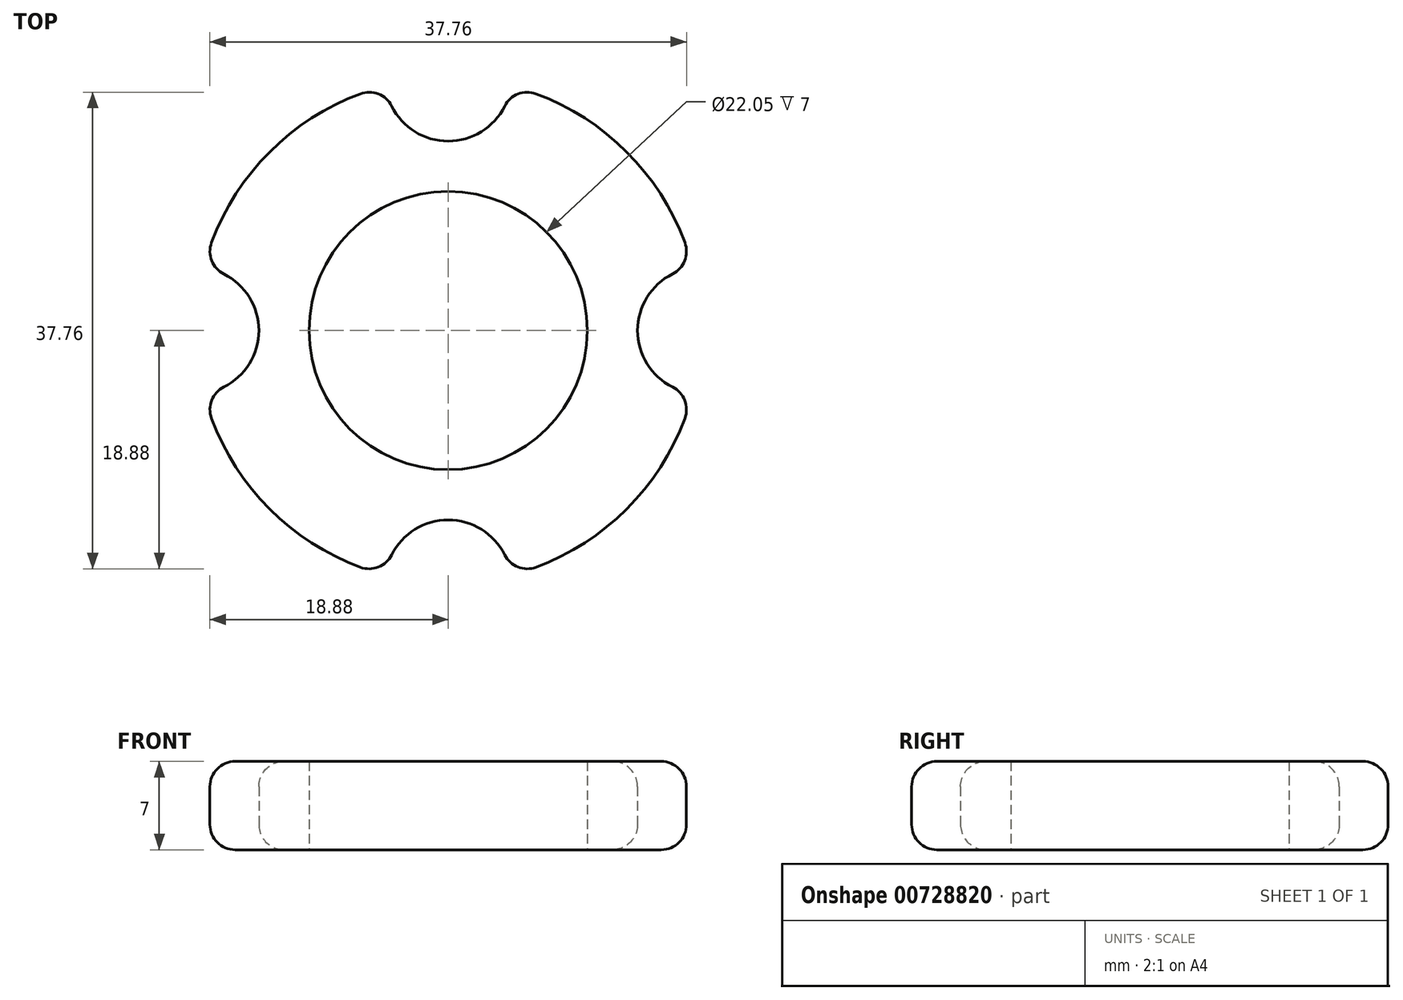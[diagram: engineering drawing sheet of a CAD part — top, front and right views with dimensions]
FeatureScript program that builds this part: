
annotation { "Feature Type Name" : "Feature", "Feature Type Description" : "" }
export const myFeature = defineFeature(function(context is Context, id is Id, definition is map)
    precondition{}
    {
        {
            var Q0;
            Q0=qCreatedBy(makeId("Top.planeOp"),FACE);
            var sketch = newSketch(context, id + "F0", { "sketchPlane" : qUnion([Q0])});
            skCircle(sketch, "E0", {"center": v(0, 0) * mm, "radius": 11.03 * mm});
            skCircle(sketch, "E1", {"center": v(0, 0) * mm, "radius": 20 * mm});
            skCircle(sketch, "E2", {"center": v(0, 20) * mm, "radius": 5 * mm});
            skCircle(sketch, "E3", {"center": v(20, 0) * mm, "radius": 5 * mm});
            skCircle(sketch, "E4", {"center": v(0, -20) * mm, "radius": 5 * mm});
            skCircle(sketch, "E5", {"center": v(-20, 0) * mm, "radius": 5 * mm});
            skSolve(sketch);
        }
        {
            var Q0;
            Q0=makeQuery(id+"F0.imprint","IMPRINT",FACE,{"disambiguationData":[TD([[makeQuery(id+"F0.imprint","IMPRINT",EDGE,{"derivedFrom":sQuery(id+"F0.wireOp",EDGE,"E0")}),-1.0]])]});
            extrude(context, id + "F1", {"entities" : qUnion([Q0]), "depth" : 7 * mm, "offsetDistance" : 25 * mm});
        }
        {
            var Q0;
            {var subQ0=sQuery(id+"F0.wireOp",EDGE,"E1");Q0=makeQuery(id+"F1.opExtrude","CAP_EDGE",EDGE,{"disambiguationData":[OSD([subQ0]),TDD([makeQuery(id+"F0.imprint","IMPRINT",EDGE,{"disambiguationData":[TD([[makeQuery(id+"F0.imprint","INTERSECT",VERTEX,{"disambiguationData":[OD(1.0)],"derivedFrom":[subQ0,sQuery(id+"F0.wireOp",EDGE,"E4")]}),-1.0]])],"derivedFrom":subQ0})])],"isStart":false});}
            var Q1;
            Q1=makeQuery(id+"F1.opExtrude","CAP_EDGE",EDGE,{"disambiguationData":[OSD([sQuery(id+"F0.wireOp",EDGE,"E4")])],"isStart":false});
            var Q2;
            {var subQ0=sQuery(id+"F0.wireOp",EDGE,"E1");Q2=makeQuery(id+"F1.opExtrude","CAP_EDGE",EDGE,{"disambiguationData":[OSD([subQ0]),TDD([makeQuery(id+"F0.imprint","IMPRINT",EDGE,{"disambiguationData":[TD([[makeQuery(id+"F0.imprint","INTERSECT",VERTEX,{"disambiguationData":[OD(1.0)],"derivedFrom":[subQ0,sQuery(id+"F0.wireOp",EDGE,"E5")]}),-1.0]])],"derivedFrom":subQ0})])],"isStart":false});}
            var Q3;
            Q3=makeQuery(id+"F1.opExtrude","CAP_EDGE",EDGE,{"disambiguationData":[OSD([sQuery(id+"F0.wireOp",EDGE,"E5")])],"isStart":false});
            var Q4;
            {var subQ0=sQuery(id+"F0.wireOp",EDGE,"E1");Q4=makeQuery(id+"F1.opExtrude","CAP_EDGE",EDGE,{"disambiguationData":[OSD([subQ0]),TDD([makeQuery(id+"F0.imprint","IMPRINT",EDGE,{"disambiguationData":[TD([[makeQuery(id+"F0.imprint","INTERSECT",VERTEX,{"disambiguationData":[OD(1.0)],"derivedFrom":[subQ0,sQuery(id+"F0.wireOp",EDGE,"E2")]}),-1.0]])],"derivedFrom":subQ0})])],"isStart":false});}
            var Q5;
            Q5=makeQuery(id+"F1.opExtrude","CAP_EDGE",EDGE,{"disambiguationData":[OSD([sQuery(id+"F0.wireOp",EDGE,"E2")])],"isStart":false});
            var Q6;
            {var subQ0=sQuery(id+"F0.wireOp",EDGE,"E1");Q6=makeQuery(id+"F1.opExtrude","CAP_EDGE",EDGE,{"disambiguationData":[OSD([subQ0]),TDD([makeQuery(id+"F0.imprint","IMPRINT",EDGE,{"disambiguationData":[TD([[makeQuery(id+"F0.imprint","INTERSECT",VERTEX,{"disambiguationData":[OD(0.0)],"derivedFrom":[subQ0,sQuery(id+"F0.wireOp",EDGE,"E2")]}),1.0]])],"derivedFrom":subQ0})])],"isStart":false});}
            var Q7;
            Q7=makeQuery(id+"F1.opExtrude","CAP_EDGE",EDGE,{"disambiguationData":[OSD([sQuery(id+"F0.wireOp",EDGE,"E3")])],"isStart":false});
            var Q8;
            {var subQ0=sQuery(id+"F0.wireOp",EDGE,"E4");var subQ1=sQuery(id+"F0.wireOp",EDGE,"E1");Q8=makeQuery(id+"F1.opExtrude","SWEPT_EDGE",EDGE,{"disambiguationData":[OSD([subQ1,subQ0]),TDD([makeQuery(id+"F0.imprint","INTERSECT",VERTEX,{"disambiguationData":[OD(0.0)],"derivedFrom":[subQ1,subQ0]})])]});}
            var Q9;
            {var subQ0=sQuery(id+"F0.wireOp",EDGE,"E4");var subQ1=sQuery(id+"F0.wireOp",EDGE,"E1");Q9=makeQuery(id+"F1.opExtrude","SWEPT_EDGE",EDGE,{"disambiguationData":[OSD([subQ1,subQ0]),TDD([makeQuery(id+"F0.imprint","INTERSECT",VERTEX,{"disambiguationData":[OD(1.0)],"derivedFrom":[subQ1,subQ0]})])]});}
            var Q10;
            {var subQ0=sQuery(id+"F0.wireOp",EDGE,"E1");Q10=makeQuery(id+"F1.opExtrude","CAP_EDGE",EDGE,{"disambiguationData":[OSD([subQ0]),TDD([makeQuery(id+"F0.imprint","IMPRINT",EDGE,{"disambiguationData":[TD([[makeQuery(id+"F0.imprint","INTERSECT",VERTEX,{"disambiguationData":[OD(1.0)],"derivedFrom":[subQ0,sQuery(id+"F0.wireOp",EDGE,"E4")]}),-1.0]])],"derivedFrom":subQ0})])],"isStart":true});}
            var Q11;
            Q11=makeQuery(id+"F1.opExtrude","CAP_EDGE",EDGE,{"disambiguationData":[OSD([sQuery(id+"F0.wireOp",EDGE,"E4")])],"isStart":true});
            var Q12;
            {var subQ0=sQuery(id+"F0.wireOp",EDGE,"E1");Q12=makeQuery(id+"F1.opExtrude","CAP_EDGE",EDGE,{"disambiguationData":[OSD([subQ0]),TDD([makeQuery(id+"F0.imprint","IMPRINT",EDGE,{"disambiguationData":[TD([[makeQuery(id+"F0.imprint","INTERSECT",VERTEX,{"disambiguationData":[OD(1.0)],"derivedFrom":[subQ0,sQuery(id+"F0.wireOp",EDGE,"E5")]}),-1.0]])],"derivedFrom":subQ0})])],"isStart":true});}
            var Q13;
            {var subQ0=sQuery(id+"F0.wireOp",EDGE,"E1");Q13=makeQuery(id+"F1.opExtrude","SWEPT_FACE",FACE,{"disambiguationData":[OSD([subQ0]),TDD([makeQuery(id+"F0.imprint","IMPRINT",EDGE,{"disambiguationData":[TD([[makeQuery(id+"F0.imprint","INTERSECT",VERTEX,{"disambiguationData":[OD(1.0)],"derivedFrom":[subQ0,sQuery(id+"F0.wireOp",EDGE,"E4")]}),-1.0]])],"derivedFrom":subQ0})])]});}
            var Q14;
            Q14=makeQuery(id+"F1.opExtrude","CAP_EDGE",EDGE,{"disambiguationData":[OSD([sQuery(id+"F0.wireOp",EDGE,"E3")])],"isStart":true});
            var Q15;
            {var subQ0=sQuery(id+"F0.wireOp",EDGE,"E3");var subQ1=sQuery(id+"F0.wireOp",EDGE,"E1");Q15=makeQuery(id+"F1.opExtrude","SWEPT_EDGE",EDGE,{"disambiguationData":[OSD([subQ1,subQ0]),TDD([makeQuery(id+"F0.imprint","INTERSECT",VERTEX,{"disambiguationData":[OD(0.0)],"derivedFrom":[subQ1,subQ0]})])]});}
            var Q16;
            {var subQ0=sQuery(id+"F0.wireOp",EDGE,"E1");Q16=makeQuery(id+"F1.opExtrude","CAP_EDGE",EDGE,{"disambiguationData":[OSD([subQ0]),TDD([makeQuery(id+"F0.imprint","IMPRINT",EDGE,{"disambiguationData":[TD([[makeQuery(id+"F0.imprint","INTERSECT",VERTEX,{"disambiguationData":[OD(0.0)],"derivedFrom":[subQ0,sQuery(id+"F0.wireOp",EDGE,"E2")]}),1.0]])],"derivedFrom":subQ0})])],"isStart":true});}
            var Q17;
            Q17=makeQuery(id+"F1.opExtrude","CAP_EDGE",EDGE,{"disambiguationData":[OSD([sQuery(id+"F0.wireOp",EDGE,"E2")])],"isStart":true});
            var Q18;
            {var subQ0=sQuery(id+"F0.wireOp",EDGE,"E2");var subQ1=sQuery(id+"F0.wireOp",EDGE,"E1");Q18=makeQuery(id+"F1.opExtrude","SWEPT_EDGE",EDGE,{"disambiguationData":[OSD([subQ1,subQ0]),TDD([makeQuery(id+"F0.imprint","INTERSECT",VERTEX,{"disambiguationData":[OD(0.0)],"derivedFrom":[subQ1,subQ0]})])]});}
            var Q19;
            {var subQ0=sQuery(id+"F0.wireOp",EDGE,"E2");var subQ1=sQuery(id+"F0.wireOp",EDGE,"E1");Q19=makeQuery(id+"F1.opExtrude","SWEPT_EDGE",EDGE,{"disambiguationData":[OSD([subQ1,subQ0]),TDD([makeQuery(id+"F0.imprint","INTERSECT",VERTEX,{"disambiguationData":[OD(1.0)],"derivedFrom":[subQ1,subQ0]})])]});}
            var Q20;
            {var subQ0=sQuery(id+"F0.wireOp",EDGE,"E1");Q20=makeQuery(id+"F1.opExtrude","CAP_EDGE",EDGE,{"disambiguationData":[OSD([subQ0]),TDD([makeQuery(id+"F0.imprint","IMPRINT",EDGE,{"disambiguationData":[TD([[makeQuery(id+"F0.imprint","INTERSECT",VERTEX,{"disambiguationData":[OD(1.0)],"derivedFrom":[subQ0,sQuery(id+"F0.wireOp",EDGE,"E2")]}),-1.0]])],"derivedFrom":subQ0})])],"isStart":true});}
            var Q21;
            {var subQ0=sQuery(id+"F0.wireOp",EDGE,"E5");var subQ1=sQuery(id+"F0.wireOp",EDGE,"E1");Q21=makeQuery(id+"F1.opExtrude","SWEPT_EDGE",EDGE,{"disambiguationData":[OSD([subQ1,subQ0]),TDD([makeQuery(id+"F0.imprint","INTERSECT",VERTEX,{"disambiguationData":[OD(0.0)],"derivedFrom":[subQ1,subQ0]})])]});}
            var Q22;
            Q22=makeQuery(id+"F1.opExtrude","CAP_EDGE",EDGE,{"disambiguationData":[OSD([sQuery(id+"F0.wireOp",EDGE,"E5")])],"isStart":true});
            var Q23;
            {var subQ0=sQuery(id+"F0.wireOp",EDGE,"E5");var subQ1=sQuery(id+"F0.wireOp",EDGE,"E1");Q23=makeQuery(id+"F1.opExtrude","SWEPT_EDGE",EDGE,{"disambiguationData":[OSD([subQ1,subQ0]),TDD([makeQuery(id+"F0.imprint","INTERSECT",VERTEX,{"disambiguationData":[OD(1.0)],"derivedFrom":[subQ1,subQ0]})])]});}
            fillet(context, id + "F2", {"entities" : qUnion([Q0, Q1, Q2, Q3, Q4, Q5, Q6, Q7, Q8, Q9, Q10, Q11, Q12, Q13, Q14, Q15, Q16, Q17, Q18, Q19, Q20, Q21, Q22, Q23]), "radius" : 2 * mm, "tangentPropagation" : true, "allowEdgeOverflow" : false});
        }
    });
